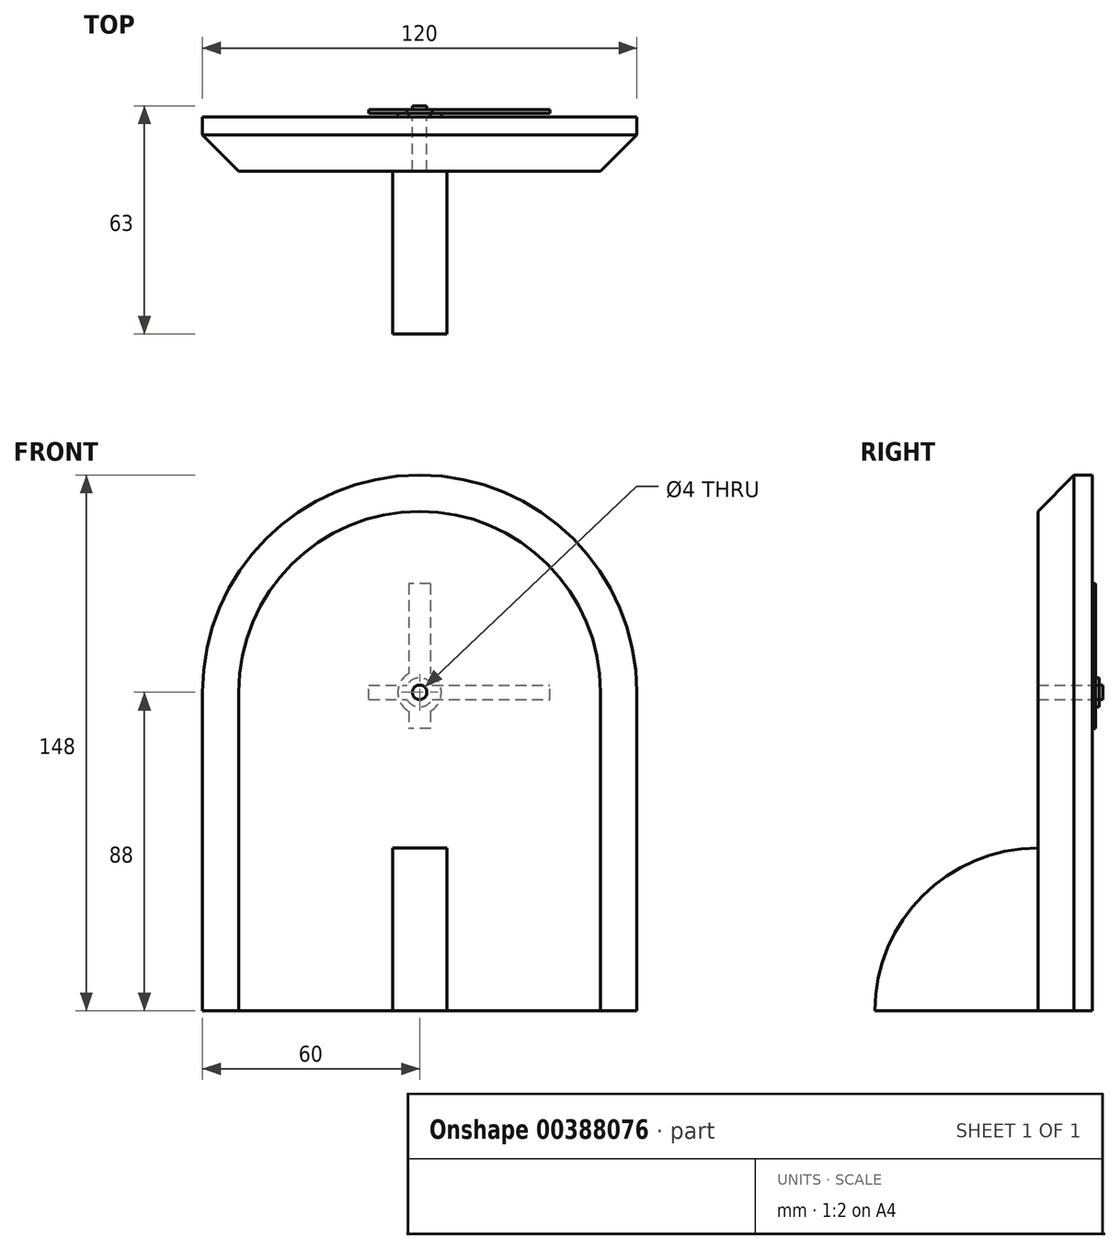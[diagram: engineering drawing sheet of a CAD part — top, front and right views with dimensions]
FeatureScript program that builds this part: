
annotation { "Feature Type Name" : "Feature", "Feature Type Description" : "" }
export const myFeature = defineFeature(function(context is Context, id is Id, definition is map)
    precondition{}
    {
        {
            var Q0;
            Q0=qCreatedBy(makeId("Front.planeOp"),FACE);
            var sketch = newSketch(context, id + "F0", { "sketchPlane" : qUnion([Q0])});
            skLineSegment(sketch, "E0", {"start": v(-60, 0) * mm, "end": v(-60, 88) * mm});
            skLineSegment(sketch, "E1", {"start": v(60, 0) * mm, "end": v(60, 88) * mm});
            skLineSegment(sketch, "E2", {"start": v(-60, 0) * mm, "end": v(60, 0) * mm});
            skArc(sketch, "E3", {"start": v(60, 88) * mm, "mid": v(0, 148) * mm, "end": v(-60, 88) * mm});
            skLineSegment(sketch, "E4", {"start": v(60, 88) * mm, "end": v(-60, 88) * mm, "construction": true});
            skCircle(sketch, "E5", {"center": v(0, 88) * mm, "radius": 2 * mm});
            skPoint(sketch, "E6.middle", {"position": v(0, 20) * mm});
            skSolve(sketch);
        }
        {
            var Q0;
            Q0=makeQuery(id+"F0.imprint","IMPRINT",FACE,{"disambiguationData":[TD([[makeQuery(id+"F0.imprint","IMPRINT",EDGE,{"derivedFrom":sQuery(id+"F0.wireOp",EDGE,"E0")}),-1.0]])]});
            extrude(context, id + "F1", {"entities" : qUnion([Q0]), "depth" : 15 * mm});
        }
        {
            var Q0;
            Q0=qCreatedBy(makeId("Right.planeOp"),FACE);
            var sketch = newSketch(context, id + "F2", { "sketchPlane" : qUnion([Q0])});
            skLineSegment(sketch, "E7", {"start": v(-15, 5) * mm, "end": v(-15, 15) * mm});
            skLineSegment(sketch, "E8", {"start": v(-15, 15) * mm, "end": v(-25, 15) * mm});
            skLineSegment(sketch, "E9", {"start": v(-25, 15) * mm, "end": v(-25, 14.12) * mm});
            skLineSegment(sketch, "E10", {"start": v(-25, 14.12) * mm, "end": v(-15.88, 14.12) * mm});
            skLineSegment(sketch, "E11", {"start": v(-15.88, 14.13) * mm, "end": v(-15.88, 5) * mm});
            skLineSegment(sketch, "E12", {"start": v(-15.88, 5) * mm, "end": v(-15, 5) * mm});
            skSolve(sketch);
        }
        {
            var Q0;
            Q0=makeQuery(id+"F1.opExtrude","CAP_FACE",FACE,{"disambiguationData":[OSD([sQuery(id+"F0.wireOp",EDGE,"E0"),sQuery(id+"F0.wireOp",EDGE,"E1"),sQuery(id+"F0.wireOp",EDGE,"E2"),sQuery(id+"F0.wireOp",EDGE,"E3"),sQuery(id+"F0.wireOp",EDGE,"E5")])],"isStart":true});
            var sketch = newSketch(context, id + "F3", { "sketchPlane" : qUnion([Q0])});
            skCircle(sketch, "E13", {"center": v(0, 88) * mm, "radius": 6 * mm});
            skLineSegment(sketch, "E14.bottom", {"start": v(-3, 118) * mm, "end": v(3, 118) * mm});
            skLineSegment(sketch, "E14.top", {"start": v(-3, 78) * mm, "end": v(3, 78) * mm});
            skLineSegment(sketch, "E14.left", {"start": v(-3, 118) * mm, "end": v(-3, 78) * mm});
            skLineSegment(sketch, "E14.right", {"start": v(3, 118) * mm, "end": v(3, 78) * mm});
            skLineSegment(sketch, "E15", {"start": v(0, 118) * mm, "end": v(0, 78) * mm, "construction": true});
            skSolve(sketch);
        }
        {
            var Q0;
            Q0 = qSketchRegion(id + "F3", true);
            extrude(context, id + "F4", {"entities" : qUnion([Q0]), "depth" : 1 * mm});
        }
        {
            var Q0;
            Q0=makeQuery(id+"F4.opExtrude","CAP_FACE",FACE,{"disambiguationData":[OSD([sQuery(id+"F3.wireOp",EDGE,"E13"),sQuery(id+"F3.wireOp",EDGE,"E14.bottom"),sQuery(id+"F3.wireOp",EDGE,"E14.top"),sQuery(id+"F3.wireOp",EDGE,"E14.left"),sQuery(id+"F3.wireOp",EDGE,"E14.right")])],"isStart":false});
            var sketch = newSketch(context, id + "F5", { "sketchPlane" : qUnion([Q0])});
            skCircle(sketch, "E16", {"center": v(0, 88) * mm, "radius": 4 * mm});
            skLineSegment(sketch, "E17.bottom", {"start": v(14, 86) * mm, "end": v(-36, 86) * mm});
            skLineSegment(sketch, "E17.top", {"start": v(14, 90) * mm, "end": v(-36, 90) * mm});
            skLineSegment(sketch, "E17.left", {"start": v(14, 86) * mm, "end": v(14, 90) * mm});
            skLineSegment(sketch, "E17.right", {"start": v(-36, 86) * mm, "end": v(-36, 90) * mm});
            skLineSegment(sketch, "E18", {"start": v(-36, 88) * mm, "end": v(14, 88) * mm, "construction": true});
            skSolve(sketch);
        }
        {
            var Q0;
            Q0 = qSketchRegion(id + "F5", true);
            extrude(context, id + "F6", {"entities" : qUnion([Q0]), "depth" : 1 * mm});
        }
        {
            var Q0;
            Q0=makeQuery(id+"F6.opExtrude","CAP_FACE",FACE,{"disambiguationData":[OSD([sQuery(id+"F5.wireOp",EDGE,"E16"),sQuery(id+"F5.wireOp",EDGE,"E17.bottom"),sQuery(id+"F5.wireOp",EDGE,"E17.top"),sQuery(id+"F5.wireOp",EDGE,"E17.left"),sQuery(id+"F5.wireOp",EDGE,"E17.right")])],"isStart":false});
            var sketch = newSketch(context, id + "F7", { "sketchPlane" : qUnion([Q0])});
            skCircle(sketch, "E19", {"center": v(0, 88) * mm, "radius": 2 * mm});
            skSolve(sketch);
        }
        {
            var Q0;
            Q0 = qSketchRegion(id + "F7", true);
            extrude(context, id + "F8", {"entities" : qUnion([Q0]), "depth" : 1 * mm});
        }
        {
            var Q0;
            Q0=makeQuery(id+"F1.opExtrude","CAP_EDGE",EDGE,{"disambiguationData":[OSD([sQuery(id+"F0.wireOp",EDGE,"E3")])],"isStart":false});
            chamfer(context, id + "F9", {"entities" : qUnion([Q0]), "width" : 10 * mm, "tangentPropagation" : true});
        }
        {
            var Q0;
            Q0=qCreatedBy(makeId("Right.planeOp"),FACE);
            var sketch = newSketch(context, id + "F10", { "sketchPlane" : qUnion([Q0])});
            skLineSegment(sketch, "E20", {"start": v(-15, 0) * mm, "end": v(-60, 0) * mm});
            skArc(sketch, "E21", {"start": v(-15, 45) * mm, "mid": v(-46.82, 31.82) * mm, "end": v(-60, 0) * mm});
            skLineSegment(sketch, "E22", {"start": v(-15, 0) * mm, "end": v(-15, 45) * mm});
            skLineSegment(sketch, "E23", {"start": v(-60, 0) * mm, "end": v(-60, -10.97) * mm, "construction": true});
            skLineSegment(sketch, "E24", {"start": v(-15, 45) * mm, "end": v(19.6, 45) * mm, "construction": true});
            skSolve(sketch);
        }
        {
            var Q0;
            Q0 = qSketchRegion(id + "F10", true);
            extrude(context, id + "F11", {"entities" : qUnion([Q0]), "endBound" : BoundingType.SYMMETRIC, "depth" : 15 * mm});
        }
    });
